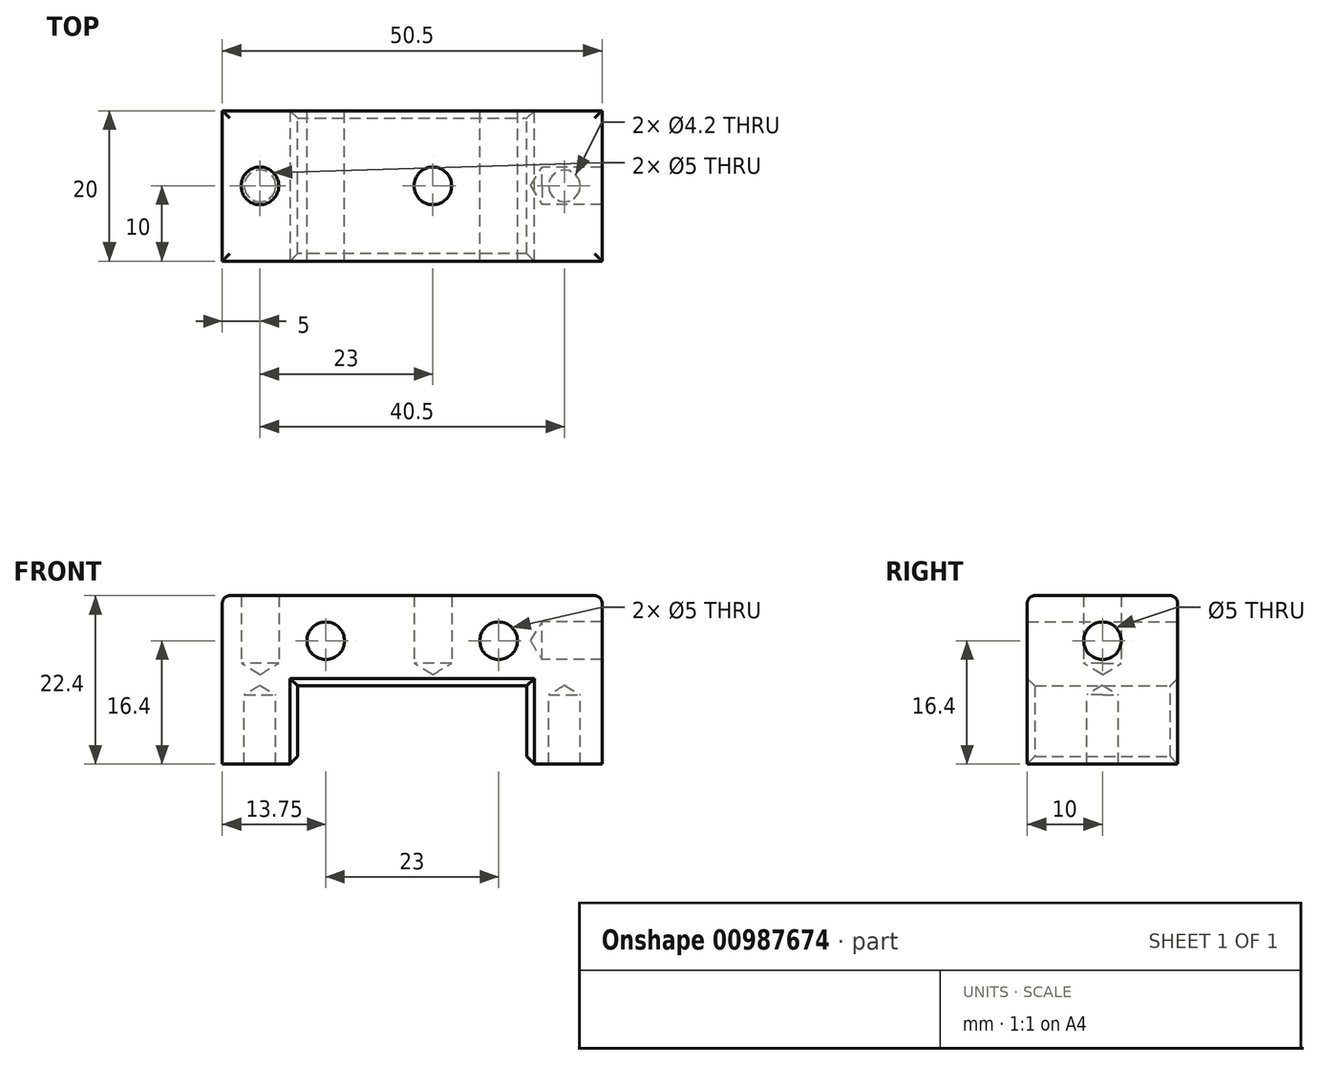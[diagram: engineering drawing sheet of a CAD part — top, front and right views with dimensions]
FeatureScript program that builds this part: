
annotation { "Feature Type Name" : "Feature", "Feature Type Description" : "" }
export const myFeature = defineFeature(function(context is Context, id is Id, definition is map)
    precondition{}
    {
        {
            var Q0;
            Q0=qCreatedBy(makeId("Front.planeOp"),FACE);
            var sketch = newSketch(context, id + "F0", { "sketchPlane" : qUnion([Q0])});
            skLineSegment(sketch, "E0", {"start": v(-25.25, -22.4) * mm, "end": v(-25.25, 0) * mm});
            skLineSegment(sketch, "E1", {"start": v(-25.25, 0) * mm, "end": v(25.25, 0) * mm});
            skLineSegment(sketch, "E2", {"start": v(25.25, 0) * mm, "end": v(25.25, -22.4) * mm});
            skLineSegment(sketch, "E3", {"start": v(25.25, -22.4) * mm, "end": v(15.25, -22.4) * mm});
            skLineSegment(sketch, "E4", {"start": v(15.25, -22.4) * mm, "end": v(15.25, -12) * mm});
            skLineSegment(sketch, "E5", {"start": v(15.25, -12) * mm, "end": v(-15.25, -12) * mm});
            skLineSegment(sketch, "E6", {"start": v(-15.25, -12) * mm, "end": v(-15.25, -22.4) * mm});
            skLineSegment(sketch, "E7", {"start": v(-15.25, -22.4) * mm, "end": v(-25.25, -22.4) * mm});
            skSolve(sketch);
        }
        {
            var Q0;
            Q0=makeQuery(id+"F0.imprint","IMPRINT",FACE,{"disambiguationData":[TD([[makeQuery(id+"F0.imprint","IMPRINT",EDGE,{"derivedFrom":sQuery(id+"F0.wireOp",EDGE,"E0")}),-1.0]])]});
            extrude(context, id + "F1", {"entities" : qUnion([Q0]), "depth" : 20 * mm, "offsetDistance" : 25 * mm, "symmetric" : true});
        }
        {
            var Q0;
            Q0=makeQuery(id+"F1.opExtrude","SWEPT_FACE",FACE,{"disambiguationData":[OSD([sQuery(id+"F0.wireOp",EDGE,"E2")])]});
            var sketch = newSketch(context, id + "F2", { "sketchPlane" : qUnion([Q0])});
            skPoint(sketch, "E8", {"position": v(0, -6) * mm});
            skSolve(sketch);
        }
        {
            var Q0;
            Q0=sQuery(id+"F2.wireOp",VERTEX,"d08d461d-1262-4413-a93d-ed473737c3a6");
            var Q1;
            Q1=sQuery(id+"F2.wireOp",VERTEX,"E8");
            var Q2;
            Q2=sQuery(id+"FTNZte6MafLFmdX_1.wireOp",VERTEX,"d9e33021-cafa-492a-8f49-9de8b4339cb5");
            var Q3;
            Q3=makeQuery(id+"F1.opExtrude","SWEPT_BODY",BODY,{"disambiguationData":[OSD([sQuery(id+"F0.wireOp",EDGE,"E0"),sQuery(id+"F0.wireOp",EDGE,"E1"),sQuery(id+"F0.wireOp",EDGE,"E2"),sQuery(id+"F0.wireOp",EDGE,"E3"),sQuery(id+"F0.wireOp",EDGE,"E4"),sQuery(id+"F0.wireOp",EDGE,"E5"),sQuery(id+"F0.wireOp",EDGE,"E6"),sQuery(id+"F0.wireOp",EDGE,"E7")])]});
            hole(context, id + "F3", {"style" : HoleStyle.SIMPLE, "endStyle" : HoleEndStyle.BLIND, "standardTappedOrClearance" : lookupTablePath({ "standard" : "ISO", "engagement" : "75%", "pitch" : "1 mm", "size" : "M6", "type" : "Tapped" }), "standardBlindInLast" : lookupTablePath({ "standard" : "ISO", "fit" : "Normal", "engagement" : "75%", "pitch" : "1 mm", "size" : "M6", "type" : "Clearance & tapped" }), "holeDiameter" : 5 * mm, "majorDiameter" : 6 * mm, "showTappedDepth" : true, "holeDepth" : 8 * mm, "isTappedThrough" : true, "tappedDepth" : 7 * mm, "tapClearance" : 1, "locations" : qUnion([Q0, Q1, Q2]), "scope" : qUnion([Q3]), "startStyle" : HoleStartStyle.PART});
        }
        {
            var Q0;
            Q0=makeQuery(id+"F1.opExtrude","SWEPT_FACE",FACE,{"disambiguationData":[OSD([sQuery(id+"F0.wireOp",EDGE,"E7")])]});
            var sketch = newSketch(context, id + "F4", { "sketchPlane" : qUnion([Q0])});
            skPoint(sketch, "E9", {"position": v(-20.25, 0) * mm});
            skPoint(sketch, "E10", {"position": v(20.25, 0) * mm});
            skSolve(sketch);
        }
        {
            var Q0;
            Q0=sQuery(id+"F4.wireOp",VERTEX,"E9");
            var Q1;
            Q1=sQuery(id+"F4.wireOp",VERTEX,"e6091487-3df0-4c40-86b1-ffb490b8e503");
            var Q2;
            Q2=sQuery(id+"F4.wireOp",VERTEX,"25d8340f-edf2-4a82-998f-7ccab65ba808");
            var Q3;
            Q3=sQuery(id+"F4.wireOp",VERTEX,"E10");
            var Q4;
            Q4=makeQuery(id+"F1.opExtrude","SWEPT_BODY",BODY,{"disambiguationData":[OSD([sQuery(id+"F0.wireOp",EDGE,"E0"),sQuery(id+"F0.wireOp",EDGE,"E1"),sQuery(id+"F0.wireOp",EDGE,"E2"),sQuery(id+"F0.wireOp",EDGE,"E3"),sQuery(id+"F0.wireOp",EDGE,"E4"),sQuery(id+"F0.wireOp",EDGE,"E5"),sQuery(id+"F0.wireOp",EDGE,"E6"),sQuery(id+"F0.wireOp",EDGE,"E7")])]});
            hole(context, id + "F5", {"style" : HoleStyle.SIMPLE, "endStyle" : HoleEndStyle.BLIND, "standardTappedOrClearance" : lookupTablePath({ "standard" : "ISO", "engagement" : "75%", "pitch" : "0.8 mm", "size" : "M5", "type" : "Tapped" }), "standardBlindInLast" : lookupTablePath({ "standard" : "ISO", "fit" : "Normal", "engagement" : "75%", "pitch" : "0.8 mm", "size" : "M5", "type" : "Clearance & tapped" }), "holeDiameter" : 4.2 * mm, "majorDiameter" : 5 * mm, "showTappedDepth" : true, "holeDepth" : 9.2 * mm, "isTappedThrough" : true, "tappedDepth" : 8.4 * mm, "tapClearance" : 1, "locations" : qUnion([Q0, Q1, Q2, Q3]), "scope" : qUnion([Q4]), "startStyle" : HoleStartStyle.PART});
        }
        {
            var Q0;
            Q0=makeQuery(id+"F1.opExtrude","CAP_FACE",FACE,{"disambiguationData":[OSD([sQuery(id+"F0.wireOp",EDGE,"E0"),sQuery(id+"F0.wireOp",EDGE,"E1"),sQuery(id+"F0.wireOp",EDGE,"E2"),sQuery(id+"F0.wireOp",EDGE,"E3"),sQuery(id+"F0.wireOp",EDGE,"E4"),sQuery(id+"F0.wireOp",EDGE,"E5"),sQuery(id+"F0.wireOp",EDGE,"E6"),sQuery(id+"F0.wireOp",EDGE,"E7")])],"isStart":false});
            var sketch = newSketch(context, id + "F6", { "sketchPlane" : qUnion([Q0])});
            skPoint(sketch, "E11", {"position": v(-11.5, -6) * mm});
            skPoint(sketch, "E12", {"position": v(11.5, -6) * mm});
            skPoint(sketch, "E13", {"position": v(0, -6) * mm});
            skSolve(sketch);
        }
        {
            var Q0;
            Q0=sQuery(id+"F6.wireOp",VERTEX,"E12");
            var Q1;
            Q1=sQuery(id+"F6.wireOp",VERTEX,"E11");
            var Q2;
            Q2=makeQuery(id+"F1.opExtrude","SWEPT_BODY",BODY,{"disambiguationData":[OSD([sQuery(id+"F0.wireOp",EDGE,"E0"),sQuery(id+"F0.wireOp",EDGE,"E1"),sQuery(id+"F0.wireOp",EDGE,"E2"),sQuery(id+"F0.wireOp",EDGE,"E3"),sQuery(id+"F0.wireOp",EDGE,"E4"),sQuery(id+"F0.wireOp",EDGE,"E5"),sQuery(id+"F0.wireOp",EDGE,"E6"),sQuery(id+"F0.wireOp",EDGE,"E7")])]});
            hole(context, id + "F7", {"style" : HoleStyle.SIMPLE, "endStyle" : HoleEndStyle.THROUGH, "standardTappedOrClearance" : lookupTablePath({ "standard" : "ISO", "engagement" : "75%", "pitch" : "1 mm", "size" : "M6", "type" : "Tapped" }), "standardBlindInLast" : lookupTablePath({ "standard" : "ISO", "fit" : "Normal", "engagement" : "75%", "pitch" : "1 mm", "size" : "M6", "type" : "Clearance & tapped" }), "holeDiameter" : 5 * mm, "majorDiameter" : 6 * mm, "showTappedDepth" : true, "isTappedThrough" : true, "tappedDepth" : 20 * mm, "tapClearance" : 0, "locations" : qUnion([Q0, Q1]), "scope" : qUnion([Q2]), "startStyle" : HoleStartStyle.PART});
        }
        {
            var Q0;
            Q0=makeQuery(id+"F1.opExtrude","SWEPT_FACE",FACE,{"disambiguationData":[OSD([sQuery(id+"F0.wireOp",EDGE,"E1")])]});
            var sketch = newSketch(context, id + "F8", { "sketchPlane" : qUnion([Q0])});
            skPoint(sketch, "E14", {"position": v(2.75, 0) * mm});
            skPoint(sketch, "E15", {"position": v(-20.25, 0) * mm});
            skSolve(sketch);
        }
        {
            var Q0;
            Q0=sQuery(id+"FNsAUHuAzS16gTO_1.wireOp",VERTEX,"cae96ffe-7221-43bb-a4f2-9818c722610d");
            var Q1;
            Q1=sQuery(id+"F8.wireOp",VERTEX,"E15");
            var Q2;
            Q2=sQuery(id+"F8.wireOp",VERTEX,"E14");
            var Q3;
            Q3=makeQuery(id+"F1.opExtrude","SWEPT_BODY",BODY,{"disambiguationData":[OSD([sQuery(id+"F0.wireOp",EDGE,"E0"),sQuery(id+"F0.wireOp",EDGE,"E1"),sQuery(id+"F0.wireOp",EDGE,"E2"),sQuery(id+"F0.wireOp",EDGE,"E3"),sQuery(id+"F0.wireOp",EDGE,"E4"),sQuery(id+"F0.wireOp",EDGE,"E5"),sQuery(id+"F0.wireOp",EDGE,"E6"),sQuery(id+"F0.wireOp",EDGE,"E7")])]});
            hole(context, id + "F9", {"style" : HoleStyle.SIMPLE, "endStyle" : HoleEndStyle.BLIND, "standardTappedOrClearance" : lookupTablePath({ "standard" : "ISO", "engagement" : "75%", "pitch" : "1 mm", "size" : "M6", "type" : "Tapped" }), "standardBlindInLast" : lookupTablePath({ "standard" : "ISO", "fit" : "Normal", "engagement" : "75%", "pitch" : "1 mm", "size" : "M6", "type" : "Clearance & tapped" }), "holeDiameter" : 5 * mm, "majorDiameter" : 6 * mm, "showTappedDepth" : true, "holeDepth" : 9 * mm, "tappedDepth" : 8 * mm, "tapClearance" : 1, "locations" : qUnion([Q0, Q1, Q2]), "scope" : qUnion([Q3]), "startStyle" : HoleStartStyle.PART});
        }
        {
            var Q0;
            Q0=makeQuery(id+"F1.opExtrude","SWEPT_EDGE",EDGE,{"disambiguationData":[OSD([sQuery(id+"F0.wireOp",EDGE,"E3"),sQuery(id+"F0.wireOp",EDGE,"E4")])]});
            var Q1;
            Q1=makeQuery(id+"F1.opExtrude","SWEPT_EDGE",EDGE,{"disambiguationData":[OSD([sQuery(id+"F0.wireOp",EDGE,"E6"),sQuery(id+"F0.wireOp",EDGE,"E7")])]});
            var Q2;
            Q2=makeQuery(id+"F1.opExtrude","CAP_EDGE",EDGE,{"disambiguationData":[OSD([sQuery(id+"F0.wireOp",EDGE,"E6")])],"isStart":false});
            var Q3;
            Q3=makeQuery(id+"F1.opExtrude","CAP_EDGE",EDGE,{"disambiguationData":[OSD([sQuery(id+"F0.wireOp",EDGE,"E5")])],"isStart":false});
            var Q4;
            Q4=makeQuery(id+"F1.opExtrude","CAP_EDGE",EDGE,{"disambiguationData":[OSD([sQuery(id+"F0.wireOp",EDGE,"E4")])],"isStart":false});
            var Q5;
            Q5=makeQuery(id+"F1.opExtrude","CAP_EDGE",EDGE,{"disambiguationData":[OSD([sQuery(id+"F0.wireOp",EDGE,"E5")])],"isStart":true});
            var Q6;
            Q6=makeQuery(id+"F1.opExtrude","CAP_EDGE",EDGE,{"disambiguationData":[OSD([sQuery(id+"F0.wireOp",EDGE,"E6")])],"isStart":true});
            var Q7;
            Q7=makeQuery(id+"F1.opExtrude","CAP_EDGE",EDGE,{"disambiguationData":[OSD([sQuery(id+"F0.wireOp",EDGE,"E4")])],"isStart":true});
            chamfer(context, id + "F10", {"entities" : qUnion([Q0, Q1, Q2, Q3, Q4, Q5, Q6, Q7]), "width" : 1 * mm, "tangentPropagation" : true});
        }
        {
            var Q0;
            Q0=makeQuery(id+"F1.opExtrude","CAP_EDGE",EDGE,{"disambiguationData":[OSD([sQuery(id+"F0.wireOp",EDGE,"E1")])],"isStart":true});
            var Q1;
            Q1=makeQuery(id+"F1.opExtrude","CAP_EDGE",EDGE,{"disambiguationData":[OSD([sQuery(id+"F0.wireOp",EDGE,"E1")])],"isStart":false});
            var Q2;
            Q2=makeQuery(id+"F1.opExtrude","SWEPT_EDGE",EDGE,{"disambiguationData":[OSD([sQuery(id+"F0.wireOp",EDGE,"E0"),sQuery(id+"F0.wireOp",EDGE,"E1")])]});
            var Q3;
            Q3=makeQuery(id+"F1.opExtrude","SWEPT_EDGE",EDGE,{"disambiguationData":[OSD([sQuery(id+"F0.wireOp",EDGE,"E1"),sQuery(id+"F0.wireOp",EDGE,"E2")])]});
            fillet(context, id + "F11", {"entities" : qUnion([Q0, Q1, Q2, Q3]), "radius" : 1 * mm, "tangentPropagation" : true, "defaultsChanged" : false, "vertexSettings" : [], "allowEdgeOverflow" : false});
        }
    });
